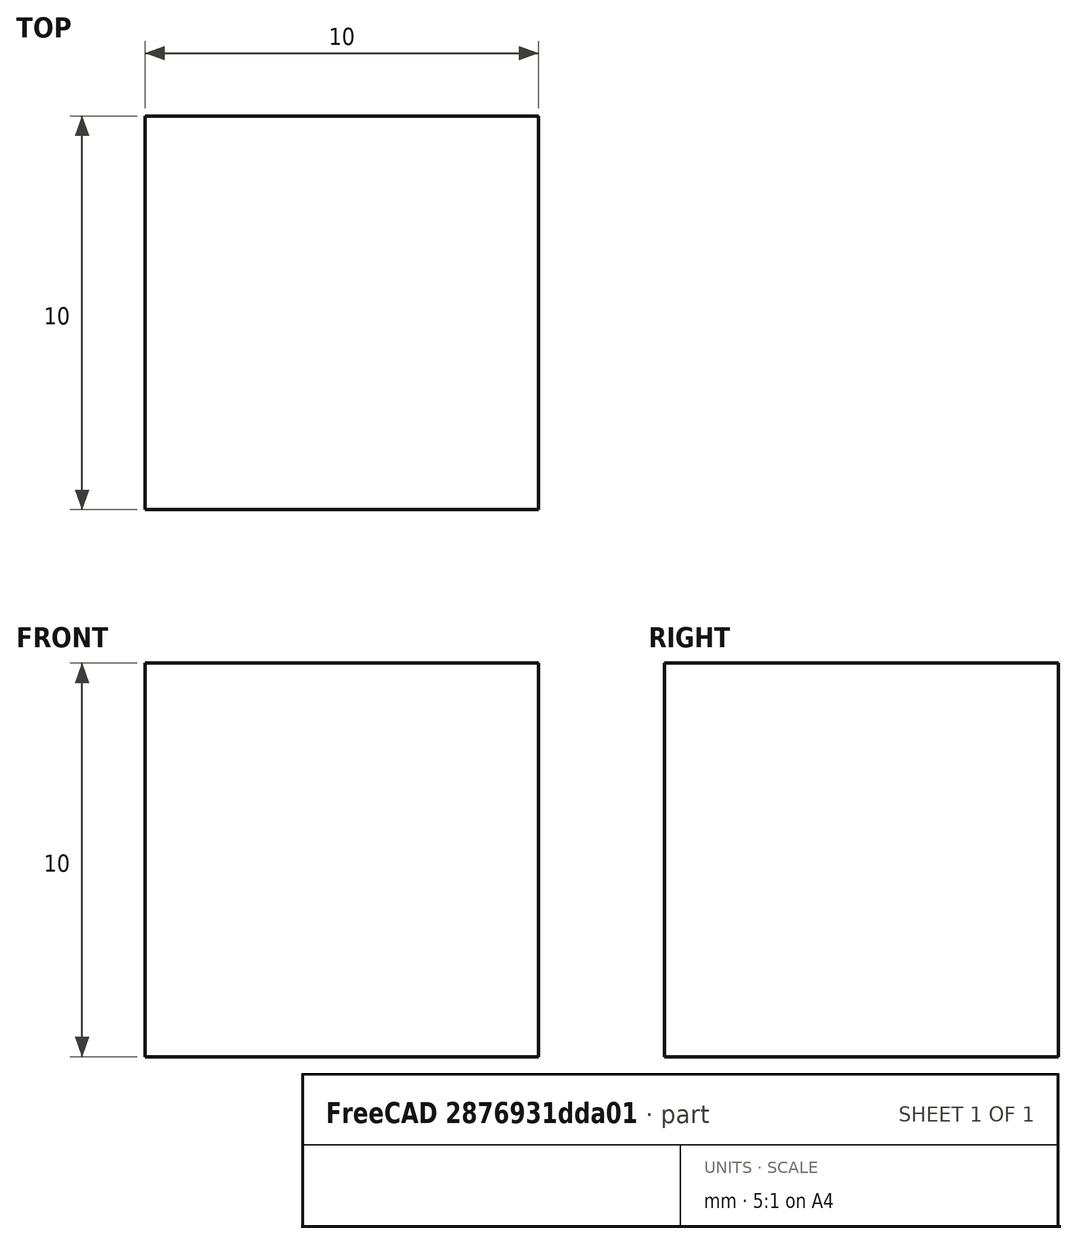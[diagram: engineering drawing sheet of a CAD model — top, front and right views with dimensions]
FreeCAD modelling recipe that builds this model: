
FCSTD DOCUMENT  (FreeCAD 0.16R6587 (Git))
Label: cube
License: All rights reserved
LicenseURL: http://en.wikipedia.org/wiki/All_rights_reserved
objects: Part::Box×1, Fem::FemMeshObject×1, Fem::ConstraintFixed×1, Fem::ConstraintPressure×1, Fem::FemSolverObjectPython×1, App::MaterialObjectPython×1, Fem::ConstraintForce×1, Fem::FemResultObject×1, Fem::FemAnalysisPython×1
note: 1 computed .brp shape members not serialized (recipe doc carries the construction recipe); baked Part::Feature solids carry a one-line shape summary decoded from their .brp

FEATURE [Part::Box] Box  label="Cube"
  Height = 10
  Length = 10
  Width = 10
FEATURE [Fem::FemMeshObject] Box_Mesh001  label="Cube_Mesh"
FEATURE [Fem::ConstraintFixed] FemConstraintFixed
  NormalDirection = (-1,0,0)
  Normals = (9) [(-1,0,0),(-1,0,0),(-1,0,0),(-1,0,0),(-1,0,0),(-1,0,0),(-1,0,0),(-1,0,0),(-1,0,0)]
  Points = (9) [(0,10,0),(0,10,5),(0,10,10),(0,5,0),(0,5,5),(0,5,10),(0,0,0),(0,0,5),(0,0,10)]
  References = -> [Box]
FEATURE [Fem::ConstraintPressure] FemConstraintPressure
  NormalDirection = (1,0,0)
  Normals = (9) [(1,0,0),(1,0,0),(1,0,0),(1,0,0),(1,0,0),(1,0,0),(1,0,0),(1,0,0),(1,0,0)]
  Points = (9) [(10,10,0),(10,10,5),(10,10,10),(10,5,0),(10,5,5),(10,5,10),(10,0,0),(10,0,5),(10,0,10)]
  Pressure = 1000
  References = -> [Box]
FEATURE [Fem::FemSolverObjectPython] CalculiX  # FEM object (typed FeaturePython)
  AnalysisType = 0
  EigenmodeHighLimit = 1000000
  EigenmodeLowLimit = 0
  NumberOfEigenmodes = 10
  SolverType = FemSolverCalculix
FEATURE [App::MaterialObjectPython] MechanicalMaterial  # material (typed FeaturePython)
  Material = Density=7900 kg/m^3,+7 more (map truncated)
FEATURE [Fem::ConstraintForce] FemConstraintForce
  Direction = -> Box [Edge5]
  DirectionVector = (0,0,-1)
  Force = 40000
  NormalDirection = (0,0,1)
  Points = (9) [(0,0,10),(5,0,10),(10,0,10),(0,5,10),(5,5,10),(10,5,10),(0,10,10),(5,10,10),(10,10,10)]
  References = -> [Box]
  Reversed = true
FEATURE [Fem::FemResultObject] Results
  DisplacementLengths = [0,0,0,0,0.0935212,0.0650661,0.0937383,0.0650115,0,0,0,0,0,0,0,0,0,0,0,0,0.0745361,0.0826962,0.0689768,0.0932309,0.0933585,0.0934617,0.0745037,0.082832,0.068946,0.0630103,0.0635703,0.0635289,0.0558722,0.0337975,0.0757671,0.0327412,0.0164219,+243 more]
  DisplacementVectors = (280) [(0,0,0),(0,0,0),(0,0,0),(0,0,0),(-0.0675227,-0.00758014,-0.0642607),(-0.0242617,-0.0109484,-0.0593725),(-0.0677483,0.00776063,-0.0643181),+273 more]
  Eigenmode = 0
  EigenmodeFrequency = 0
  Mesh = -> Box_Mesh001
  NodeNumbers = [1,2,3,4,5,6,7,8,9,10,11,12,13,14,15,16,17,18,19,20,21,22,23,24,25,26,27,28,29,30,31,32,33,34,35,36,37,38,39,40,41,42,43,44,45,46,47,48,49,50,51,52,53,54,55,56,57,58,59,60,61,62,63,64,65,66,67,68,69,+211 more]
  Stats = [-0.0680669,-0.0225964,0.00296745,-0.0109484,1.47168e-05,0.0110702,-0.0643181,-0.0308767,0,0,0.039463,0.0937383,385.38,1006.74,2203.51]
  StressValues = [2160.52,654.381,2162.06,628.131,985.328,895.619,984.722,898.175,1058.94,1471.07,871.326,1938.32,2203.51,2125.13,1062.54,1477.57,899.691,725.548,1050.16,995.576,907.45,962.745,894.685,1008.49,998.819,994.816,922.001,966.246,892.453,905.608,+250 more]
FEATURE [Fem::FemAnalysisPython] MechanicalAnalysis  # FEM object (typed FeaturePython)
  Member = -> [CalculiX,Box_Mesh001,FemConstraintFixed,FemConstraintPressure,FemConstraintForce,MechanicalMaterial,Results]
